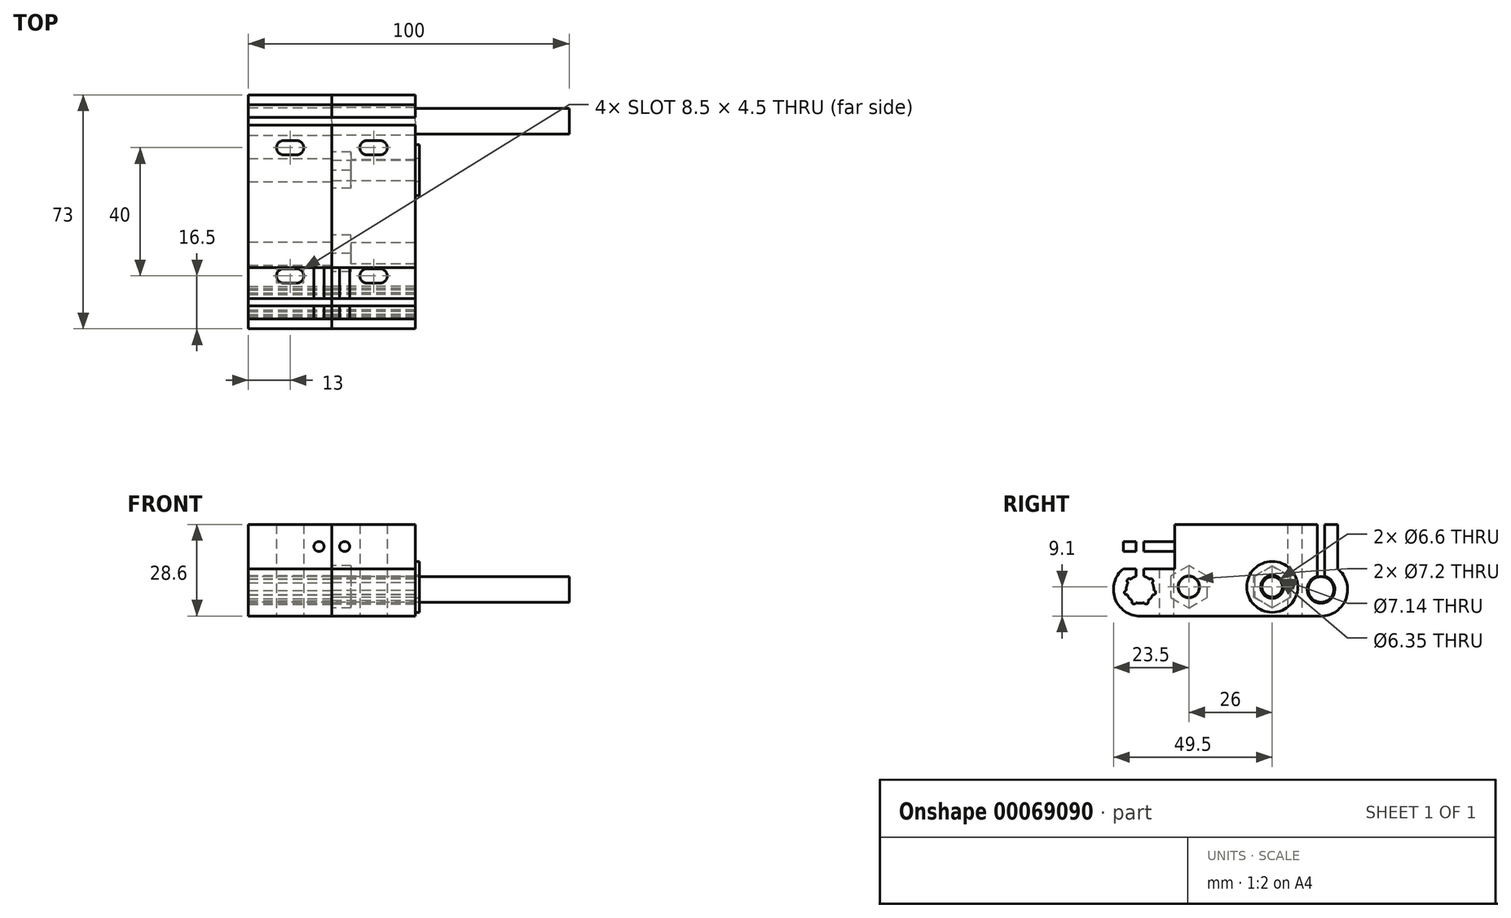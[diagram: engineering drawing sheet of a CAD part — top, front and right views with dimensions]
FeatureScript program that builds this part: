
annotation { "Feature Type Name" : "Feature", "Feature Type Description" : "" }
export const myFeature = defineFeature(function(context is Context, id is Id, definition is map)
    precondition{}
    {
        {
            var Q0;
            Q0=qCreatedBy(makeId("Right.planeOp"),FACE);
            var sketch = newSketch(context, id + "F0", { "sketchPlane" : qUnion([Q0])});
            skLineSegment(sketch, "E0", {"start": v(0, 0) * mm, "end": v(0, 28.6) * mm, "construction": true});
            skLineSegment(sketch, "E1", {"start": v(0, 0) * mm, "end": v(28.2, 0) * mm});
            skCircle(sketch, "E2", {"center": v(28.2, 8.3) * mm, "radius": 4.3 * mm});
            skLineSegment(sketch, "E3", {"start": v(0, 28.6) * mm, "end": v(27, 28.6) * mm});
            skLineSegment(sketch, "E4", {"start": v(27, 28.6) * mm, "end": v(27, 12.43) * mm});
            skArc(sketch, "E5", {"start": v(28.2, 0) * mm, "mid": v(36.03, 5.54) * mm, "end": v(33.4, 14.77) * mm});
            skLineSegment(sketch, "E6", {"start": v(28.2, 16.6) * mm, "end": v(28.2, 0) * mm, "construction": true});
            skLineSegment(sketch, "E7", {"start": v(33.4, 14.77) * mm, "end": v(33.4, 28.6) * mm});
            skLineSegment(sketch, "E8", {"start": v(33.4, 28.6) * mm, "end": v(29.4, 28.6) * mm});
            skLineSegment(sketch, "E9", {"start": v(29.4, 28.6) * mm, "end": v(29.4, 12.43) * mm});
            skCircle(sketch, "E10", {"center": v(13, 9.1) * mm, "radius": 3.3 * mm});
            skCircle(sketch, "E11.cCircle", {"center": v(13, 9.1) * mm, "radius": 5.7 * mm, "construction": true});
            skLineSegment(sketch, "E11.0", {"start": v(13, 15.68) * mm, "end": v(18.7, 12.4) * mm});
            skLineSegment(sketch, "E11.1", {"start": v(18.7, 12.4) * mm, "end": v(18.7, 5.8) * mm});
            skLineSegment(sketch, "E11.2", {"start": v(18.7, 5.8) * mm, "end": v(13, 2.52) * mm});
            skLineSegment(sketch, "E11.3", {"start": v(13, 2.52) * mm, "end": v(7.3, 5.8) * mm});
            skLineSegment(sketch, "E11.4", {"start": v(7.3, 5.8) * mm, "end": v(7.3, 12.4) * mm});
            skLineSegment(sketch, "E11.5", {"start": v(7.3, 12.4) * mm, "end": v(13, 15.68) * mm});
            skPoint(sketch, "E11.0.midPoint", {"position": v(15.85, 14.04) * mm});
            skLineSegment(sketch, "E12.MirrorCS", {"start": v(-18.7, 5.8) * mm, "end": v(-13, 2.52) * mm});
            skLineSegment(sketch, "E13.MirrorCS", {"start": v(-18.7, 12.4) * mm, "end": v(-18.7, 5.8) * mm});
            skLineSegment(sketch, "E14.MirrorCS", {"start": v(-7.3, 12.4) * mm, "end": v(-13, 15.68) * mm});
            skLineSegment(sketch, "E15.MirrorCS", {"start": v(-13, 15.68) * mm, "end": v(-18.7, 12.4) * mm});
            skLineSegment(sketch, "E16.MirrorCS", {"start": v(-7.3, 5.8) * mm, "end": v(-7.3, 12.4) * mm});
            skPoint(sketch, "E17.MirrorP", {"position": v(-15.85, 14.04) * mm});
            skLineSegment(sketch, "E18.MirrorCS", {"start": v(-29.4, 28.6) * mm, "end": v(-33.4, 28.6) * mm});
            skLineSegment(sketch, "E19.MirrorCS", {"start": v(-13, 2.52) * mm, "end": v(-7.3, 5.8) * mm});
            skLineSegment(sketch, "E20.MirrorCS", {"start": v(-29.4, 28.6) * mm, "end": v(-29.4, 12.43) * mm});
            skCircle(sketch, "E21.MirrorC", {"center": v(-13, 9.1) * mm, "radius": 3.3 * mm});
            skCircle(sketch, "E22.MirrorC", {"center": v(-13, 9.1) * mm, "radius": 5.7 * mm, "construction": true});
            skLineSegment(sketch, "E23.MirrorCS", {"start": v(0, 0) * mm, "end": v(-28.2, 0) * mm});
            skLineSegment(sketch, "E24.MirrorCS", {"start": v(-33.4, 14.77) * mm, "end": v(-33.4, 28.6) * mm});
            skLineSegment(sketch, "E25.MirrorCS", {"start": v(-27, 28.6) * mm, "end": v(-27, 12.43) * mm});
            skCircle(sketch, "E26.MirrorC", {"center": v(-28.2, 8.3) * mm, "radius": 4.3 * mm});
            skArc(sketch, "E27.MirrorCS", {"start": v(-28.2, 0) * mm, "mid": v(-36.03, 5.54) * mm, "end": v(-33.4, 14.77) * mm});
            skArc(sketch, "E28.MirrorCS", {"start": v(-27, 12.43) * mm, "mid": v(-27.73, 12.57) * mm, "end": v(-28.47, 12.6) * mm});
            skLineSegment(sketch, "E29.MirrorCS", {"start": v(0, 28.6) * mm, "end": v(-27, 28.6) * mm});
            skLineSegment(sketch, "E30", {"start": v(27, 28.6) * mm, "end": v(29.4, 28.6) * mm, "construction": true});
            skPoint(sketch, "E31", {"position": v(28.2, 28.6) * mm});
            skLineSegment(sketch, "E32", {"start": v(28.2, 12.6) * mm, "end": v(10.15, 12.6) * mm, "construction": true});
            skSolve(sketch);
        }
        {
            var Q0;
            Q0=makeQuery(id+"F0.imprint","IMPRINT",FACE,{"disambiguationData":[TD([[makeQuery(id+"F0.imprint","IMPRINT",EDGE,{"derivedFrom":sQuery(id+"F0.wireOp",EDGE,"E1")}),1.0]])]});
            var Q1;
            Q1=makeQuery(id+"F0.imprint","IMPRINT",FACE,{"disambiguationData":[TD([[makeQuery(id+"F0.imprint","IMPRINT",EDGE,{"derivedFrom":sQuery(id+"F0.wireOp",EDGE,"E12.MirrorCS")}),1.0]])]});
            var Q2;
            Q2=makeQuery(id+"F0.imprint","IMPRINT",FACE,{"disambiguationData":[TD([[makeQuery(id+"F0.imprint","IMPRINT",EDGE,{"derivedFrom":sQuery(id+"F0.wireOp",EDGE,"E10")}),-1.0]])]});
            extrude(context, id + "F1", {"entities" : qUnion([Q0, Q1, Q2]), "depth" : 26 * mm, "offsetDistance" : 25 * mm});
        }
        {
            var Q0;
            Q0=makeQuery(id+"F1.opExtrude","SWEPT_FACE",FACE,{"disambiguationData":[OSD([sQuery(id+"F0.wireOp",EDGE,"E24.MirrorCS")])]});
            var sketch = newSketch(context, id + "F2", { "sketchPlane" : qUnion([Q0])});
            skCircle(sketch, "E33", {"center": v(22, 21.68) * mm, "radius": 1.57 * mm});
            skPoint(sketch, "E33.centerSnap0", {"position": v(26, 21.68) * mm});
            skLineSegment(sketch, "E34", {"start": v(13, 28.6) * mm, "end": v(13, 14.77) * mm, "construction": true});
            skCircle(sketch, "E35.MirrorC", {"center": v(4, 21.68) * mm, "radius": 1.57 * mm});
            skSolve(sketch);
        }
        {
            var Q0;
            Q0=makeQuery(id+"F2.imprint","IMPRINT",FACE,{"disambiguationData":[TD([[makeQuery(id+"F2.imprint","IMPRINT",EDGE,{"derivedFrom":sQuery(id+"F2.wireOp",EDGE,"E33")}),1.0]])]});
            var Q1;
            Q1=makeQuery(id+"F2.imprint","IMPRINT",FACE,{"disambiguationData":[TD([[makeQuery(id+"F2.imprint","IMPRINT",EDGE,{"derivedFrom":sQuery(id+"F2.wireOp",EDGE,"E35.MirrorC")}),-1.0]])]});
            extrude(context, id + "F3", {"entities" : qUnion([Q0, Q1]), "operationType" : NewBodyOperationType.REMOVE, "oppositeDirection" : true, "depth" : 16 * mm, "offsetDistance" : 25 * mm});
        }
        {
            var Q0;
            Q0=makeQuery(id+"F1.opExtrude","SWEPT_FACE",FACE,{"disambiguationData":[OSD([sQuery(id+"F0.wireOp",EDGE,"E24.MirrorCS")])]});
            var sketch = newSketch(context, id + "F4", { "sketchPlane" : qUnion([Q0])});
            skCircle(sketch, "E36", {"center": v(4, 21.68) * mm, "radius": 3 * mm});
            skCircle(sketch, "E37", {"center": v(4, 21.68) * mm, "radius": 1.9 * mm});
            skCircle(sketch, "E38", {"center": v(22, 21.68) * mm, "radius": 1.9 * mm});
            skCircle(sketch, "E39", {"center": v(22, 21.68) * mm, "radius": 3 * mm});
            skSolve(sketch);
        }
        {
            var Q0;
            Q0=makeQuery(id+"F4.imprint","IMPRINT",FACE,{"disambiguationData":[TD([[makeQuery(id+"F4.imprint","IMPRINT",EDGE,{"derivedFrom":sQuery(id+"F4.wireOp",EDGE,"E38")}),1.0]])]});
            var Q1;
            Q1=makeQuery(id+"F4.imprint","IMPRINT",FACE,{"disambiguationData":[TD([[makeQuery(id+"F4.imprint","IMPRINT",EDGE,{"derivedFrom":sQuery(id+"F4.wireOp",EDGE,"E37")}),1.0]])]});
            extrude(context, id + "F5", {"entities" : qUnion([Q0, Q1]), "operationType" : NewBodyOperationType.REMOVE, "endBound" : BoundingType.UP_TO_NEXT, "oppositeDirection" : true, "depth" : 25 * mm, "offsetDistance" : 25 * mm});
        }
        {
            var Q0;
            Q0=makeQuery(id+"F4.imprint","IMPRINT",FACE,{"disambiguationData":[TD([[makeQuery(id+"F4.imprint","IMPRINT",EDGE,{"derivedFrom":sQuery(id+"F4.wireOp",EDGE,"E36")}),1.0]])]});
            var Q1;
            Q1=makeQuery(id+"F4.imprint","IMPRINT",FACE,{"disambiguationData":[TD([[makeQuery(id+"F4.imprint","IMPRINT",EDGE,{"derivedFrom":sQuery(id+"F4.wireOp",EDGE,"E38")}),-1.0]])]});
            extrude(context, id + "F6", {"entities" : qUnion([Q0, Q1]), "operationType" : NewBodyOperationType.REMOVE, "oppositeDirection" : true, "depth" : 1.5 * mm, "offsetDistance" : 25 * mm});
        }
        {
            var Q0;
            Q0=makeQuery(id+"F1.opExtrude","SWEPT_FACE",FACE,{"disambiguationData":[OSD([sQuery(id+"F0.wireOp",EDGE,"E1"),sQuery(id+"F0.wireOp",EDGE,"E23.MirrorCS")])]});
            var sketch = newSketch(context, id + "F7", { "sketchPlane" : qUnion([Q0])});
            skArc(sketch, "E40", {"start": v(11, -17.75) * mm, "mid": v(8.75, -20) * mm, "end": v(11, -22.25) * mm});
            skLineSegment(sketch, "E41", {"start": v(13, -28.2) * mm, "end": v(13, 28.2) * mm, "construction": true});
            skLineSegment(sketch, "E42", {"start": v(0, 0) * mm, "end": v(26, 0) * mm, "construction": true});
            skArc(sketch, "E43.MirrorCS", {"start": v(15, -17.75) * mm, "mid": v(17.25, -20) * mm, "end": v(15, -22.25) * mm});
            skLineSegment(sketch, "E44", {"start": v(11, -22.25) * mm, "end": v(15, -22.25) * mm});
            skLineSegment(sketch, "E45", {"start": v(11, -17.75) * mm, "end": v(15, -17.75) * mm});
            skLineSegment(sketch, "E46.MirrorCS", {"start": v(11, 22.25) * mm, "end": v(15, 22.25) * mm});
            skLineSegment(sketch, "E47.MirrorCS", {"start": v(11, 17.75) * mm, "end": v(15, 17.75) * mm});
            skArc(sketch, "E48.MirrorCS", {"start": v(15, 17.75) * mm, "mid": v(17.25, 20) * mm, "end": v(15, 22.25) * mm});
            skArc(sketch, "E49.MirrorCS", {"start": v(11, 17.75) * mm, "mid": v(8.75, 20) * mm, "end": v(11, 22.25) * mm});
            skSolve(sketch);
        }
        {
            var Q0;
            Q0 = qSketchRegion(id + "F7", true);
            extrude(context, id + "F8", {"entities" : qUnion([Q0]), "operationType" : NewBodyOperationType.REMOVE, "endBound" : BoundingType.THROUGH_ALL, "oppositeDirection" : true, "depth" : 25 * mm, "offsetDistance" : 25 * mm});
        }
        {
            var Q0;
            Q0=makeQuery(id+"F1.opExtrude","CAP_FACE",FACE,{"disambiguationData":[OSD([sQuery(id+"F0.wireOp",EDGE,"E1"),sQuery(id+"F0.wireOp",EDGE,"E2"),sQuery(id+"F0.wireOp",EDGE,"E3"),sQuery(id+"F0.wireOp",EDGE,"E4"),sQuery(id+"F0.wireOp",EDGE,"E5"),sQuery(id+"F0.wireOp",EDGE,"E7"),sQuery(id+"F0.wireOp",EDGE,"E8"),sQuery(id+"F0.wireOp",EDGE,"E9"),sQuery(id+"F0.wireOp",EDGE,"E10"),sQuery(id+"F0.wireOp",EDGE,"E18.MirrorCS"),sQuery(id+"F0.wireOp",EDGE,"E20.MirrorCS"),sQuery(id+"F0.wireOp",EDGE,"E21.MirrorC"),sQuery(id+"F0.wireOp",EDGE,"E23.MirrorCS"),sQuery(id+"F0.wireOp",EDGE,"E24.MirrorCS"),sQuery(id+"F0.wireOp",EDGE,"E25.MirrorCS"),sQuery(id+"F0.wireOp",EDGE,"E26.MirrorC"),sQuery(id+"F0.wireOp",EDGE,"E27.MirrorCS"),sQuery(id+"F0.wireOp",EDGE,"E29.MirrorCS")])],"isStart":true});
            var sketch = newSketch(context, id + "F9", { "sketchPlane" : qUnion([Q0])});
            skCircle(sketch, "E50", {"center": v(31.56, 10.98) * mm, "radius": 0.7 * mm});
            skCircle(sketch, "E51.1.0", {"center": v(28.2, 12.6) * mm, "radius": 0.7 * mm, "construction": true});
            skCircle(sketch, "E51.2.0", {"center": v(24.84, 10.98) * mm, "radius": 0.7 * mm});
            skCircle(sketch, "E51.3.0", {"center": v(24, 7.34) * mm, "radius": 0.7 * mm});
            skCircle(sketch, "E51.4.0", {"center": v(26.33, 4.43) * mm, "radius": 0.7 * mm});
            skCircle(sketch, "E51.5.0", {"center": v(30.07, 4.43) * mm, "radius": 0.7 * mm});
            skCircle(sketch, "E51.6.0", {"center": v(32.4, 7.34) * mm, "radius": 0.7 * mm});
            skPoint(sketch, "E51.center", {"position": v(28.2, 8.3) * mm});
            skSolve(sketch);
        }
        {
            var Q0;
            Q0 = qSketchRegion(id + "F9", true);
            extrude(context, id + "F10", {"entities" : qUnion([Q0]), "operationType" : NewBodyOperationType.REMOVE, "endBound" : BoundingType.THROUGH_ALL, "oppositeDirection" : true, "depth" : 25 * mm, "offsetDistance" : 25 * mm});
        }
        {
            var Q0;
            Q0=makeQuery(id+"F1.opExtrude","SWEPT_BODY",BODY,{"disambiguationData":[OSD([sQuery(id+"F0.wireOp",EDGE,"E1"),sQuery(id+"F0.wireOp",EDGE,"E2"),sQuery(id+"F0.wireOp",EDGE,"E3"),sQuery(id+"F0.wireOp",EDGE,"E4"),sQuery(id+"F0.wireOp",EDGE,"1242f0a4-d42f-46b1-896b-aa9933bf8ce0"),sQuery(id+"F0.wireOp",EDGE,"E5"),sQuery(id+"F0.wireOp",EDGE,"QkmVrJF1-xM3N-g0Gr-hpWV-Dd6ElclZAGtq"),sQuery(id+"F0.wireOp",EDGE,"rpgFmPdA-QWbr-rvJi-R6iS-U15gdcaVF5pK"),sQuery(id+"F0.wireOp",EDGE,"ccUqaIXa-5mzT-K7vj-ob5H-Qi0m3c9Ocldp"),sQuery(id+"F0.wireOp",EDGE,"E7"),sQuery(id+"F0.wireOp",EDGE,"E8"),sQuery(id+"F0.wireOp",EDGE,"E9"),sQuery(id+"F0.wireOp",EDGE,"E10"),sQuery(id+"F0.wireOp",EDGE,"E18.MirrorCS"),sQuery(id+"F0.wireOp",EDGE,"E20.MirrorCS"),sQuery(id+"F0.wireOp",EDGE,"E21.MirrorC"),sQuery(id+"F0.wireOp",EDGE,"E130.MirrorCS"),sQuery(id+"F0.wireOp",EDGE,"E132.MirrorCS"),sQuery(id+"F0.wireOp",EDGE,"E23.MirrorCS"),sQuery(id+"F0.wireOp",EDGE,"E24.MirrorCS"),sQuery(id+"F0.wireOp",EDGE,"E25.MirrorCS"),sQuery(id+"F0.wireOp",EDGE,"E26.MirrorC"),sQuery(id+"F0.wireOp",EDGE,"E27.MirrorCS"),sQuery(id+"F0.wireOp",EDGE,"E28.MirrorCS"),sQuery(id+"F0.wireOp",EDGE,"E29.MirrorCS"),sQuery(id+"F0.wireOp",EDGE,"E140.MirrorCS")])]});
            var Q1;
            Q1=qCreatedBy(makeId("Right.planeOp"),FACE);
            mirror(context, id + "F11", {"entities" : qUnion([Q0]), "mirrorPlane" : qUnion([Q1])});
        }
        {
            var Q0;
            Q0=makeQuery(id+"F0.imprint","IMPRINT",FACE,{"disambiguationData":[TD([[makeQuery(id+"F0.imprint","IMPRINT",EDGE,{"derivedFrom":sQuery(id+"F0.wireOp",EDGE,"E10")}),-1.0]])]});
            var Q1;
            Q1=makeQuery(id+"F0.imprint","IMPRINT",FACE,{"disambiguationData":[TD([[makeQuery(id+"F0.imprint","IMPRINT",EDGE,{"derivedFrom":sQuery(id+"F0.wireOp",EDGE,"E12.MirrorCS")}),1.0]])]});
            extrude(context, id + "F12", {"entities" : qUnion([Q0, Q1]), "operationType" : NewBodyOperationType.REMOVE, "depth" : 6 * mm, "offsetDistance" : 25 * mm});
        }
        {
            var Q0;
            Q0=makeQuery(id+"F1.opExtrude","CAP_FACE",FACE,{"disambiguationData":[OSD([sQuery(id+"F0.wireOp",EDGE,"E1"),sQuery(id+"F0.wireOp",EDGE,"E2"),sQuery(id+"F0.wireOp",EDGE,"E3"),sQuery(id+"F0.wireOp",EDGE,"E4"),sQuery(id+"F0.wireOp",EDGE,"1242f0a4-d42f-46b1-896b-aa9933bf8ce0"),sQuery(id+"F0.wireOp",EDGE,"E5"),sQuery(id+"F0.wireOp",EDGE,"QkmVrJF1-xM3N-g0Gr-hpWV-Dd6ElclZAGtq"),sQuery(id+"F0.wireOp",EDGE,"rpgFmPdA-QWbr-rvJi-R6iS-U15gdcaVF5pK"),sQuery(id+"F0.wireOp",EDGE,"ccUqaIXa-5mzT-K7vj-ob5H-Qi0m3c9Ocldp"),sQuery(id+"F0.wireOp",EDGE,"E7"),sQuery(id+"F0.wireOp",EDGE,"E8"),sQuery(id+"F0.wireOp",EDGE,"E9"),sQuery(id+"F0.wireOp",EDGE,"E10"),sQuery(id+"F0.wireOp",EDGE,"E18.MirrorCS"),sQuery(id+"F0.wireOp",EDGE,"E20.MirrorCS"),sQuery(id+"F0.wireOp",EDGE,"E21.MirrorC"),sQuery(id+"F0.wireOp",EDGE,"E130.MirrorCS"),sQuery(id+"F0.wireOp",EDGE,"E132.MirrorCS"),sQuery(id+"F0.wireOp",EDGE,"E23.MirrorCS"),sQuery(id+"F0.wireOp",EDGE,"E24.MirrorCS"),sQuery(id+"F0.wireOp",EDGE,"E25.MirrorCS"),sQuery(id+"F0.wireOp",EDGE,"E26.MirrorC"),sQuery(id+"F0.wireOp",EDGE,"E27.MirrorCS"),sQuery(id+"F0.wireOp",EDGE,"E28.MirrorCS"),sQuery(id+"F0.wireOp",EDGE,"E29.MirrorCS"),sQuery(id+"F0.wireOp",EDGE,"E140.MirrorCS")])],"isStart":false});
            var sketch = newSketch(context, id + "F13", { "sketchPlane" : qUnion([Q0])});
            skCircle(sketch, "E52", {"center": v(13, 9.1) * mm, "radius": 7.94 * mm});
            skCircle(sketch, "E53", {"center": v(13, 9.1) * mm, "radius": 3.57 * mm});
            skSolve(sketch);
        }
        {
            var Q0;
            Q0 = qSketchRegion(id + "F13", true);
            extrude(context, id + "F14", {"entities" : qUnion([Q0]), "depth" : 1.27 * mm, "offsetDistance" : 25 * mm});
        }
        {
            var Q0;
            Q0=makeQuery(id+"F14.opExtrude","CAP_FACE",FACE,{"disambiguationData":[OSD([sQuery(id+"F13.wireOp",EDGE,"E52"),sQuery(id+"F13.wireOp",EDGE,"E53")])],"isStart":false});
            var sketch = newSketch(context, id + "F15", { "sketchPlane" : qUnion([Q0])});
            skCircle(sketch, "E54.cCircle", {"center": v(13, 9.1) * mm, "radius": 5.56 * mm, "construction": true});
            skLineSegment(sketch, "E54.0", {"start": v(18.56, 12.3) * mm, "end": v(18.56, 5.9) * mm});
            skLineSegment(sketch, "E54.1", {"start": v(18.56, 5.9) * mm, "end": v(13, 2.68) * mm});
            skLineSegment(sketch, "E54.2", {"start": v(13, 2.68) * mm, "end": v(7.44, 5.9) * mm});
            skLineSegment(sketch, "E54.3", {"start": v(7.44, 5.9) * mm, "end": v(7.44, 12.3) * mm});
            skLineSegment(sketch, "E54.4", {"start": v(7.44, 12.3) * mm, "end": v(13, 15.52) * mm});
            skLineSegment(sketch, "E54.5", {"start": v(13, 15.52) * mm, "end": v(18.56, 12.3) * mm});
            skPoint(sketch, "E54.0.midPoint", {"position": v(18.56, 9.1) * mm});
            skCircle(sketch, "E55", {"center": v(13, 9.1) * mm, "radius": 3.18 * mm});
            skSolve(sketch);
        }
        {
            var Q0;
            Q0=makeQuery(id+"F15.imprint","IMPRINT",FACE,{"disambiguationData":[TD([[makeQuery(id+"F15.imprint","IMPRINT",EDGE,{"derivedFrom":sQuery(id+"F15.wireOp",EDGE,"E55")}),1.0]])]});
            extrude(context, id + "F16", {"entities" : qUnion([Q0]), "oppositeDirection" : true, "depth" : 104 * mm, "offsetDistance" : 25 * mm});
        }
        {
            var Q0;
            Q0=makeQuery(id+"F12.boolean.opBoolean","COPY",FACE,{"derivedFrom":makeQuery(id+"F12.opExtrude","CAP_FACE",FACE,{"disambiguationData":[OSD([sQuery(id+"F0.wireOp",EDGE,"E10"),sQuery(id+"F0.wireOp",EDGE,"E11.0"),sQuery(id+"F0.wireOp",EDGE,"E11.1"),sQuery(id+"F0.wireOp",EDGE,"E11.2"),sQuery(id+"F0.wireOp",EDGE,"E11.3"),sQuery(id+"F0.wireOp",EDGE,"E11.4"),sQuery(id+"F0.wireOp",EDGE,"E11.5")])],"isStart":false})});
            var sketch = newSketch(context, id + "F17", { "sketchPlane" : qUnion([Q0])});
            skCircle(sketch, "E56", {"center": v(-13, 9.1) * mm, "radius": 3.18 * mm});
            skCircle(sketch, "E57.cCircle", {"center": v(-13, 9.1) * mm, "radius": 5.56 * mm, "construction": true});
            skLineSegment(sketch, "E57.0", {"start": v(-7.44, 12.3) * mm, "end": v(-7.44, 5.9) * mm});
            skLineSegment(sketch, "E57.1", {"start": v(-7.44, 5.9) * mm, "end": v(-13, 2.68) * mm});
            skLineSegment(sketch, "E57.2", {"start": v(-13, 2.68) * mm, "end": v(-18.56, 5.9) * mm});
            skLineSegment(sketch, "E57.3", {"start": v(-18.56, 5.9) * mm, "end": v(-18.56, 12.3) * mm});
            skLineSegment(sketch, "E57.4", {"start": v(-18.56, 12.3) * mm, "end": v(-13, 15.52) * mm});
            skLineSegment(sketch, "E57.5", {"start": v(-13, 15.52) * mm, "end": v(-7.44, 12.3) * mm});
            skPoint(sketch, "E57.0.midPoint", {"position": v(-7.44, 9.1) * mm});
            skSolve(sketch);
        }
        {
            var Q0;
            Q0 = qSketchRegion(id + "F17", true);
            extrude(context, id + "F18", {"entities" : qUnion([Q0]), "depth" : 7 / 812.8 * mm, "offsetDistance" : 25 * mm});
        }
        {
            var Q0;
            Q0=makeQuery(id+"F11.opPattern","COPY",FACE,{"derivedFrom":makeQuery(id+"F1.opExtrude","CAP_FACE",FACE,{"disambiguationData":[OSD([sQuery(id+"F0.wireOp",EDGE,"E1"),sQuery(id+"F0.wireOp",EDGE,"E2"),sQuery(id+"F0.wireOp",EDGE,"E3"),sQuery(id+"F0.wireOp",EDGE,"E4"),sQuery(id+"F0.wireOp",EDGE,"1242f0a4-d42f-46b1-896b-aa9933bf8ce0"),sQuery(id+"F0.wireOp",EDGE,"E5"),sQuery(id+"F0.wireOp",EDGE,"QkmVrJF1-xM3N-g0Gr-hpWV-Dd6ElclZAGtq"),sQuery(id+"F0.wireOp",EDGE,"rpgFmPdA-QWbr-rvJi-R6iS-U15gdcaVF5pK"),sQuery(id+"F0.wireOp",EDGE,"ccUqaIXa-5mzT-K7vj-ob5H-Qi0m3c9Ocldp"),sQuery(id+"F0.wireOp",EDGE,"E7"),sQuery(id+"F0.wireOp",EDGE,"E8"),sQuery(id+"F0.wireOp",EDGE,"E9"),sQuery(id+"F0.wireOp",EDGE,"E10"),sQuery(id+"F0.wireOp",EDGE,"E18.MirrorCS"),sQuery(id+"F0.wireOp",EDGE,"E20.MirrorCS"),sQuery(id+"F0.wireOp",EDGE,"E21.MirrorC"),sQuery(id+"F0.wireOp",EDGE,"E130.MirrorCS"),sQuery(id+"F0.wireOp",EDGE,"E132.MirrorCS"),sQuery(id+"F0.wireOp",EDGE,"E23.MirrorCS"),sQuery(id+"F0.wireOp",EDGE,"E24.MirrorCS"),sQuery(id+"F0.wireOp",EDGE,"E25.MirrorCS"),sQuery(id+"F0.wireOp",EDGE,"E26.MirrorC"),sQuery(id+"F0.wireOp",EDGE,"E27.MirrorCS"),sQuery(id+"F0.wireOp",EDGE,"E28.MirrorCS"),sQuery(id+"F0.wireOp",EDGE,"E29.MirrorCS"),sQuery(id+"F0.wireOp",EDGE,"E140.MirrorCS")])],"isStart":false}),"instanceName":"1"});
            var sketch = newSketch(context, id + "F19", { "sketchPlane" : qUnion([Q0])});
            skCircle(sketch, "E58", {"center": v(-28.2, 8.3) * mm, "radius": 4 * mm});
            skSolve(sketch);
        }
        {
            var Q0;
            Q0 = qSketchRegion(id + "F19", true);
            extrude(context, id + "F20", {"entities" : qUnion([Q0]), "oppositeDirection" : true, "depth" : 100 * mm, "offsetDistance" : 25 * mm});
        }
        {
            var Q0;
            Q0=makeQuery(id+"F11.opPattern","COPY",FACE,{"derivedFrom":makeQuery(id+"F1.opExtrude","CAP_FACE",FACE,{"disambiguationData":[OSD([sQuery(id+"F0.wireOp",EDGE,"E1"),sQuery(id+"F0.wireOp",EDGE,"E2"),sQuery(id+"F0.wireOp",EDGE,"E3"),sQuery(id+"F0.wireOp",EDGE,"E4"),sQuery(id+"F0.wireOp",EDGE,"E5"),sQuery(id+"F0.wireOp",EDGE,"E7"),sQuery(id+"F0.wireOp",EDGE,"E8"),sQuery(id+"F0.wireOp",EDGE,"E9"),sQuery(id+"F0.wireOp",EDGE,"E10"),sQuery(id+"F0.wireOp",EDGE,"E18.MirrorCS"),sQuery(id+"F0.wireOp",EDGE,"E20.MirrorCS"),sQuery(id+"F0.wireOp",EDGE,"E21.MirrorC"),sQuery(id+"F0.wireOp",EDGE,"E23.MirrorCS"),sQuery(id+"F0.wireOp",EDGE,"E24.MirrorCS"),sQuery(id+"F0.wireOp",EDGE,"E25.MirrorCS"),sQuery(id+"F0.wireOp",EDGE,"E26.MirrorC"),sQuery(id+"F0.wireOp",EDGE,"E27.MirrorCS"),sQuery(id+"F0.wireOp",EDGE,"E29.MirrorCS")])],"isStart":true}),"instanceName":"1"});
            var sketch = newSketch(context, id + "F21", { "sketchPlane" : qUnion([Q0])});
            skCircle(sketch, "E59", {"center": v(-13, 9.1) * mm, "radius": 3.6 * mm});
            skCircle(sketch, "E60", {"center": v(13, 9.1) * mm, "radius": 3.6 * mm});
            skSolve(sketch);
        }
        {
            var Q0;
            Q0 = qSketchRegion(id + "F21", true);
            extrude(context, id + "F22", {"entities" : qUnion([Q0]), "operationType" : NewBodyOperationType.REMOVE, "endBound" : BoundingType.THROUGH_ALL, "oppositeDirection" : true, "depth" : 25 * mm, "offsetDistance" : 25 * mm});
        }
    });
